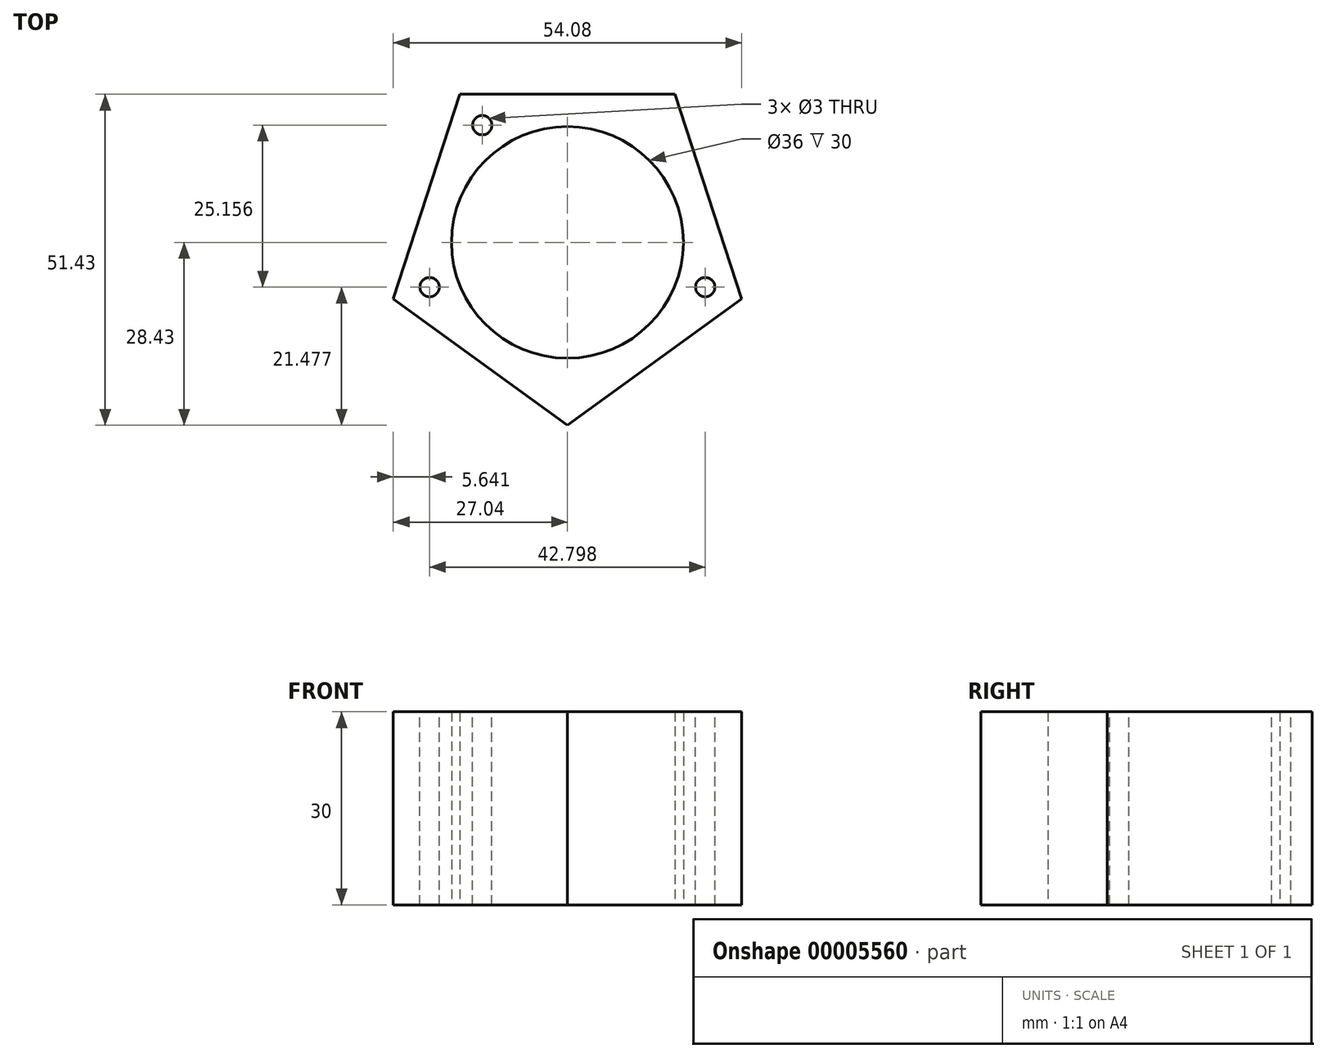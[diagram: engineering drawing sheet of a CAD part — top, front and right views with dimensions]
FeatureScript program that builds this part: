
annotation { "Feature Type Name" : "Feature", "Feature Type Description" : "" }
export const myFeature = defineFeature(function(context is Context, id is Id, definition is map)
    precondition{}
    {
        {
            var Q0;
            Q0=qCreatedBy(makeId("Top.planeOp"),FACE);
            var sketch = newSketch(context, id + "F0", { "sketchPlane" : qUnion([Q0])});
            skCircle(sketch, "E0", {"center": v(0, 0) * mm, "radius": 18 * mm});
            skCircle(sketch, "E1.cCircle", {"center": v(0, 0) * mm, "radius": 23 * mm, "construction": true});
            skLineSegment(sketch, "E1.0", {"start": v(-16.71, 23) * mm, "end": v(16.71, 23) * mm});
            skLineSegment(sketch, "E1.1", {"start": v(16.71, 23) * mm, "end": v(27.04, -8.79) * mm});
            skLineSegment(sketch, "E1.2", {"start": v(27.04, -8.79) * mm, "end": v(0, -28.43) * mm});
            skLineSegment(sketch, "E1.3", {"start": v(0, -28.43) * mm, "end": v(-27.04, -8.79) * mm});
            skLineSegment(sketch, "E1.4", {"start": v(-27.04, -8.79) * mm, "end": v(-16.71, 23) * mm});
            skPoint(sketch, "E1.0.midPoint", {"position": v(0, 23) * mm});
            skSolve(sketch);
        }
        {
            var Q0;
            Q0 = qSketchRegion(id + "F0", true);
            extrude(context, id + "F1", {"entities" : qUnion([Q0]), "depth" : 30 * mm});
        }
        {
            var Q0;
            Q0=makeQuery(id+"F1.opExtrude","CAP_FACE",FACE,{"disambiguationData":[OSD([sQuery(id+"F0.wireOp",EDGE,"E0"),sQuery(id+"F0.wireOp",EDGE,"E1.0"),sQuery(id+"F0.wireOp",EDGE,"E1.1"),sQuery(id+"F0.wireOp",EDGE,"E1.2"),sQuery(id+"F0.wireOp",EDGE,"E1.3"),sQuery(id+"F0.wireOp",EDGE,"E1.4")])],"isStart":false});
            var sketch = newSketch(context, id + "F2", { "sketchPlane" : qUnion([Q0])});
            skCircle(sketch, "E2", {"center": v(0, -22.5) * mm, "radius": 1.5 * mm});
            skCircle(sketch, "E3.1.0", {"center": v(-21.4, -6.95) * mm, "radius": 1.5 * mm});
            skCircle(sketch, "E3.2.0", {"center": v(-13.23, 18.2) * mm, "radius": 1.5 * mm});
            skCircle(sketch, "E3.3.0", {"center": v(13.23, 18.2) * mm, "radius": 1.5 * mm});
            skCircle(sketch, "E3.4.0", {"center": v(21.4, -6.95) * mm, "radius": 1.5 * mm});
            skPoint(sketch, "E3.center", {"position": v(0, 0) * mm});
            skLineSegment(sketch, "E3.anchor1", {"start": v(0, 0) * mm, "end": v(0, -22.5) * mm, "construction": true});
            skLineSegment(sketch, "E3.anchor2", {"start": v(0, 0) * mm, "end": v(21.4, -6.95) * mm, "construction": true});
            skCircle(sketch, "E4.cCircle", {"center": v(0, 0) * mm, "radius": 40.47 * mm, "construction": true});
            skLineSegment(sketch, "E4.0", {"start": v(-29.4, 40.47) * mm, "end": v(29.4, 40.47) * mm});
            skLineSegment(sketch, "E4.1", {"start": v(29.4, 40.47) * mm, "end": v(47.58, -15.46) * mm});
            skLineSegment(sketch, "E4.2", {"start": v(47.58, -15.46) * mm, "end": v(0, -50.03) * mm});
            skLineSegment(sketch, "E4.3", {"start": v(0, -50.03) * mm, "end": v(-47.58, -15.46) * mm});
            skLineSegment(sketch, "E4.4", {"start": v(-47.58, -15.46) * mm, "end": v(-29.4, 40.47) * mm});
            skPoint(sketch, "E4.0.midPoint", {"position": v(0, 40.47) * mm});
            skSolve(sketch);
        }
        {
            var Q0;
            Q0=makeQuery(id+"F2.imprint","IMPRINT",FACE,{"disambiguationData":[TD([[makeQuery(id+"F2.imprint","IMPRINT",EDGE,{"derivedFrom":sQuery(id+"F2.wireOp",EDGE,"E3.2.0")}),1.0]])]});
            var Q1;
            Q1=makeQuery(id+"F2.imprint","IMPRINT",FACE,{"disambiguationData":[TD([[makeQuery(id+"F2.imprint","IMPRINT",EDGE,{"derivedFrom":sQuery(id+"F2.wireOp",EDGE,"E3.4.0")}),1.0]])]});
            var Q2;
            Q2=makeQuery(id+"F2.imprint","IMPRINT",FACE,{"disambiguationData":[TD([[makeQuery(id+"F2.imprint","IMPRINT",EDGE,{"derivedFrom":sQuery(id+"F2.wireOp",EDGE,"E3.1.0")}),1.0]])]});
            extrude(context, id + "F3", {"entities" : qUnion([Q0, Q1, Q2]), "operationType" : NewBodyOperationType.REMOVE, "endBound" : BoundingType.THROUGH_ALL, "oppositeDirection" : true, "depth" : 8 * mm});
        }
    });
